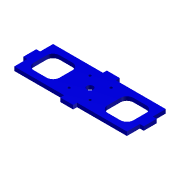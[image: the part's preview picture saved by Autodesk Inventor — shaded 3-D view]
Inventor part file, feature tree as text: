
AUTODESK INVENTOR PART (.ipt)
format: ipt  version: 2012 (Build 160160000, 160)  size: 138,240 bytes
history: native  units: mm
features: extrude x1, sketch x1
ambient origin geometry x8: Origin, YZ Plane, XZ Plane, XY Plane, X Axis, Y Axis, Z Axis, Center Point
bodies: Solid1 (feature_tree)
feature tree (2):
  extrude  "Extrusion1"  Depth=10.0mm
  sketch  "Sketch1"  dims[d0=10.0mm d1=10.0mm d2=10.0mm d3=10.0mm d4=10.0mm d5=10.0mm d6=38.5mm d7=38.5mm d8=10.0mm d9=38.5mm d10=10.0mm d11=38.5mm d12=5.0mm d13=5.0mm d15=5.0mm d16=20.0mm d17=5.0mm d18=5.0mm d19=5.0mm d20=20.0mm d21=3.0mm d22=3.0mm d23=3.0mm d24=3.0mm d25=5.0mm d26=5.0mm d27=5.0mm d28=15.0mm d30=2.0mm d32=40.0mm d34=360.0deg d36=3.0mm d37=0.0mm]
